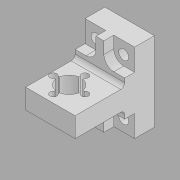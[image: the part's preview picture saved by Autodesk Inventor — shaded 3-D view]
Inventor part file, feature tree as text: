
AUTODESK INVENTOR PART (.ipt)
format: ipt  version: 2020.2 (Build 242310000, 310)  size: 212,480 bytes
history: native  units: mm
features: extrude x5, sketch x5, mirror x2, hole x1, fillet x1, pattern_circular x1
ambient origin geometry x8: Origin, YZ Plane, XZ Plane, XY Plane, X Axis, Y Axis, Z Axis, Center Point
bodies: Solid1 (feature_tree)
feature tree (15):
  extrude  "Extrusion1"  Depth=25.0mm
  hole  "Hole1"  [1 undecoded]
  extrude  "Extrusion3"  Depth=6.0mm
  extrude  "Extrusion4"  Depth=25.0mm TaperAngle=0.0deg
  fillet  "Fillet2"  Radius=12.0mm
  extrude  "Extrusion5"  Depth=12.0mm
  mirror  "Mirror1"
  mirror  "Mirror2"
  extrude  "Extrusion6"  Depth=15.0mm
  pattern_circular  "Circular Pattern1"  [2 undecoded]
  sketch  "Sketch1"  dims[d0=40.0mm d1=25.0mm]
  sketch  "Sketch4"  dims[d2=15.0mm d3=0.0mm]
  sketch  "Sketch5"  dims[d9=5.0mm d10=6.0mm d11=10.0mm d12=5.0mm d13=90.0deg d14=8.0mm d15=20.594885mm d20=10.0mm]
  sketch  "Sketch6"  dims[d21=6.0mm d22=6.0mm]
  sketch  "Sketch7"  dims[d24=5.5mm d25=25.0mm d26=0.0mm d27=12.0mm d28=12.0mm d29=15.0mm d30=3.5mm d31=8.0mm d32=40.0mm d34=360.0deg d36=0.0mm d37=0.0mm d38=2.0mm d39=25.0mm d40=0.0mm d41=1.0mm d42=1.0mm d43=15.0mm d44=0.0mm d45=40.0mm d46=360.0deg]
note: 3 required parameter values undecoded (feature->parameter linkage not recoverable at this tier; creation-order binding heuristic only, values carry confidence <= 0.55)
